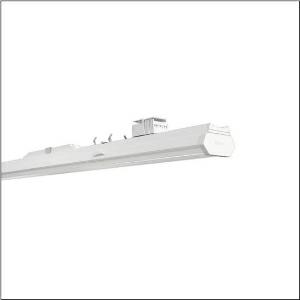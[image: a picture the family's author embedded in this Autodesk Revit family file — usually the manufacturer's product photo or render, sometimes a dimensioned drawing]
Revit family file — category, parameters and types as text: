
# Revit family: licross_r__21_protected_ho_52td12dn4e5md_1fe0
name_source: partatom
category: Lighting Fixtures
units: mm (PartAtom-declared; Revit-internal decimal feet)

## family parameters
Cut with Voids When Loaded = No
Host = Face
Light Source = No
Part Type = Normal
Room Calculation Point = No
Round Connector Dimension = Use Diameter
Shared = No

## types (1)
- --- (1 x LED, 2200 lm, 14.2 W, 4000K)
    Apparent Load = 14 VA
    CIE Flux Codes = 70 91 97 98 100
    Color Rendering = 80
    Color Temperature = 4000K
    Default Elevation = 1800 mm
    Description = Licross® 21 Protected HO, luminaire insert, of sheet steel, galvanised, coil coated, white, length: 1.500mm, width: 90mm, height: 103mm, LED rated luminous flux: 14.690lm, light colour: 840, control gear: DALI 2 (for two DALI lines), with plug, 6-pole, with phase selection, mains connection: 220..240V, AC/DC, 0/50..60Hz, rated input power: 85W, without changeover relay, for emergency light function, for central battery installations according to DIN EN 60598-2-22, halogen-free wiring, primary light control with lens, of plastic, primary optical cover: cover, of PMMA, light emission: direct distribution, primary light characteristic: symmetric, protection rating (complete): IP54, insulation class (complete): insulation class I (protective earthing), certification: CE, ENEC, VDE, UKCA, protection symbol: D if used in an environment with non-conductive dust loads with corresponding accessories, impact resistance: IK06, permissible ambient temperature for indoor applications: -25..+35°C, standard: EN 60598-2-22, corresponds to IFS (International Featured Standards) requirements for safety and quality in the food industry, reducing of maximum allowable ambient temperature of 5°C with ceiling mounting, LABS conformity tested according to VDMA 24364:2018-05, packaging unit: 1 piece
    Height = 92 mm
    Lamp = 1 x LED
    Lamp Light Flux = 2200 lm
    Lamp Power = 14.2 W
    Lamp count = 1
    Length = 1500 mm
    Luminous efficacy = 155 lm/W
    Manufacturer = Siteco
    ModVariant = No
    Model = 52TD12DN4E5MD
    Mounting Place = Ceiling
    Mounting Type = Pendant
    Number of Poles = 1
    OnlyDefault = Yes
    Power Factor = 1
    Product Name = Licross® 21 Protected HO
    Product group = luminaire insert
    ProductGroupID = 902
    Protection Class = Protection class I
    Protection Degree = IP 54
    RLX_Detail_Level = 1
    RLX_Emergency_Light_Flux = 0 lm
    RLX_Emergency_Type = 0
    RLX_Emergency_Type_DB = No
    RlxData = <blob elided: 24893 chars, md5=3d53dc35>
    Socket = socket
    Standby Power = 0 W
    System Light Flux = 2200 lm
    System Power = 14 W
    Type Comments = : DC mode (central or group accumulator) initial emergency light level
    Type Image = l_1256148.jpg
    URL = http://relux.com
    VarID = @adj_116348
    Voltage = 0 V
    Weight = 0.00 kg
    Width = 88 mm

## geometry (parser evidence)
native form markers: Blend x4, Sweep x9
no freeform markers — native parametric forms only
